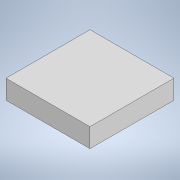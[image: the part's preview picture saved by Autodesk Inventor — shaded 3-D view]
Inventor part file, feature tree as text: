
AUTODESK INVENTOR PART (.ipt)
format: ipt  version: 2021 (Build 250183000, 183)  size: 5,541,888 bytes
history: native  units: mm
features: other x21, fillet x14, surface_op x12, sketch x9, extrude x6, revolve x4, plane x3, pattern_circular x2, loft x1
ambient origin geometry x8: Origin, YZ Plane, XZ Plane, XY Plane, X Axis, Y Axis, Z Axis, Center Point
bodies: Solid1 (feature_tree)
feature tree (72):
  plane  "Work Plane1"
  plane  "Work Plane2"
  plane  "Work Plane3"
  surface_op  "Trim1"
  surface_op  "Trim2"
  surface_op  "Trim3"
  surface_op  "Trim4"
  fillet  "Fillet5"  Radius=138.0mm
  fillet  "Fillet6"  Radius=95.0mm
  fillet  "Fillet7"  Radius=33.0mm
  fillet  "Fillet8"  Radius=110.0mm
  fillet  "Fillet9"  Radius=200.0mm
  fillet  "Fillet10"  Radius=463.0mm
  pattern_circular  "Circular Pattern1"  Count=3  [1 undecoded]
  surface_op  "Stitch Surface1"
  pattern_circular  "Circular Pattern2"  Count=20  [1 undecoded]
  surface_op  "Trim5"
  surface_op  "Trim6"
  surface_op  "Trim7"
  surface_op  "Trim8"
  surface_op  "Trim9"
  surface_op  "Stitch Surface2"
  extrude  "Extrusion1"  Depth=16.0mm
  sketch  "Sketch1"  dims[d6=84.0mm]
  other  "Srf1"
  sketch  "Sketch2"  dims[d7=12.566371mm d8=30.0mm]
  other  "Srf2"
  sketch  "Sketch3"  dims[d9=35.0mm d10=200.0mm]
  other  "Srf3"
  sketch  "Sketch7"  dims[d11=12.566371mm d12=16.0mm]
  sketch  "Sketch9"  dims[d13=50.0mm d14=130.0mm]
  sketch  "Sketch10"  dims[d15=245.0mm d16=369.0mm]
  other  "Srf4"
  other  "Srf5"
  other  "Srf6"
  sketch  "Sketch11"  dims[d17=63.0mm d18=12.566371mm]
  other  "Srf7"
  other  "Srf8"
  other  "Srf9"
  other  "Srf11"
  other  "Srf12"
  other  "Srf13"
  other  "Srf10"
  other  "Srf14"
  sketch  "Sketch12"  dims[d42=152.0mm d43=80.0mm d44=80.0mm]
  other  "Srf15"
  other  "Srf16"
  other  "Srf17"
  other  "Srf18"
  other  "Srf19"
  other  "Srf20"
  other  "Srf21"
  sketch  "Sketch13"  dims[d45=100.0mm d46=6.283185mm d47=6.283185mm d48=45.0mm d49=360.0mm d51=25.0mm d52=50.0mm d53=0.0mm d54=90.0deg d55=0.0mm d56=90.0deg d57=0.0mm d58=90.0deg d59=120.0mm d61=-25.0mm d62=-120.0mm d63=15.0mm d64=15.0mm d65=20.0mm d66=75.0mm d67=30.0mm d68=70.0mm d69=30.0mm d70=80.0mm d71=12.566371mm d72=5.0mm d73=5.0mm d74=5.0mm d75=5.0mm d76=5.0mm d77=5.0mm d78=5.0mm d79=5.0mm d80=50.0mm d81=360.0deg d83=300.0mm d84=80.0mm d85=10.0mm d86=0.0mm d87=50.0mm d88=360.0deg d90=5.0mm d91=5.0mm d92=5.0mm d93=5.0mm d94=5.0mm d96=0.0mm d97=5.0mm d98=1100.0mm d99=550.0mm d100=250.0mm d101=68.0mm d102=1100.0mm d103=0.0mm]
  revolve  "RevolutionSrf1"  [1 undecoded]
  revolve  "RevolutionSrf2"  [1 undecoded]
  revolve  "RevolutionSrf3"  [1 undecoded]
  loft  "LoftSrf1"
  fillet  "Fillet4"  Radius=80.0mm
  extrude  "ExtrusionSrf1"  Depth=6.283185mm
  fillet  "Fillet1"  Radius=6.283185mm
  fillet  "Fillet2"  Radius=45.0mm
  revolve  "RevolutionSrf4"  [1 undecoded]
  fillet  "Fillet3"  Radius=25.0mm
  fillet  "Fillet11"  Radius=50.0mm
  fillet  "Fillet12"  [1 undecoded]
  fillet  "Fillet13"  [1 undecoded]
  fillet  "Fillet14"  [1 undecoded]
  extrude  "ExtrusionSrf2"  Depth=120.0mm
  extrude  "ExtrusionSrf3"  Depth=15.0mm
  extrude  "ExtrusionSrf4"  Depth=15.0mm
  extrude  "ExtrusionSrf5"  Depth=20.0mm
  surface_op  "Boundary Patch1"
note: 9 required parameter values undecoded (feature->parameter linkage not recoverable at this tier; creation-order binding heuristic only, values carry confidence <= 0.55)